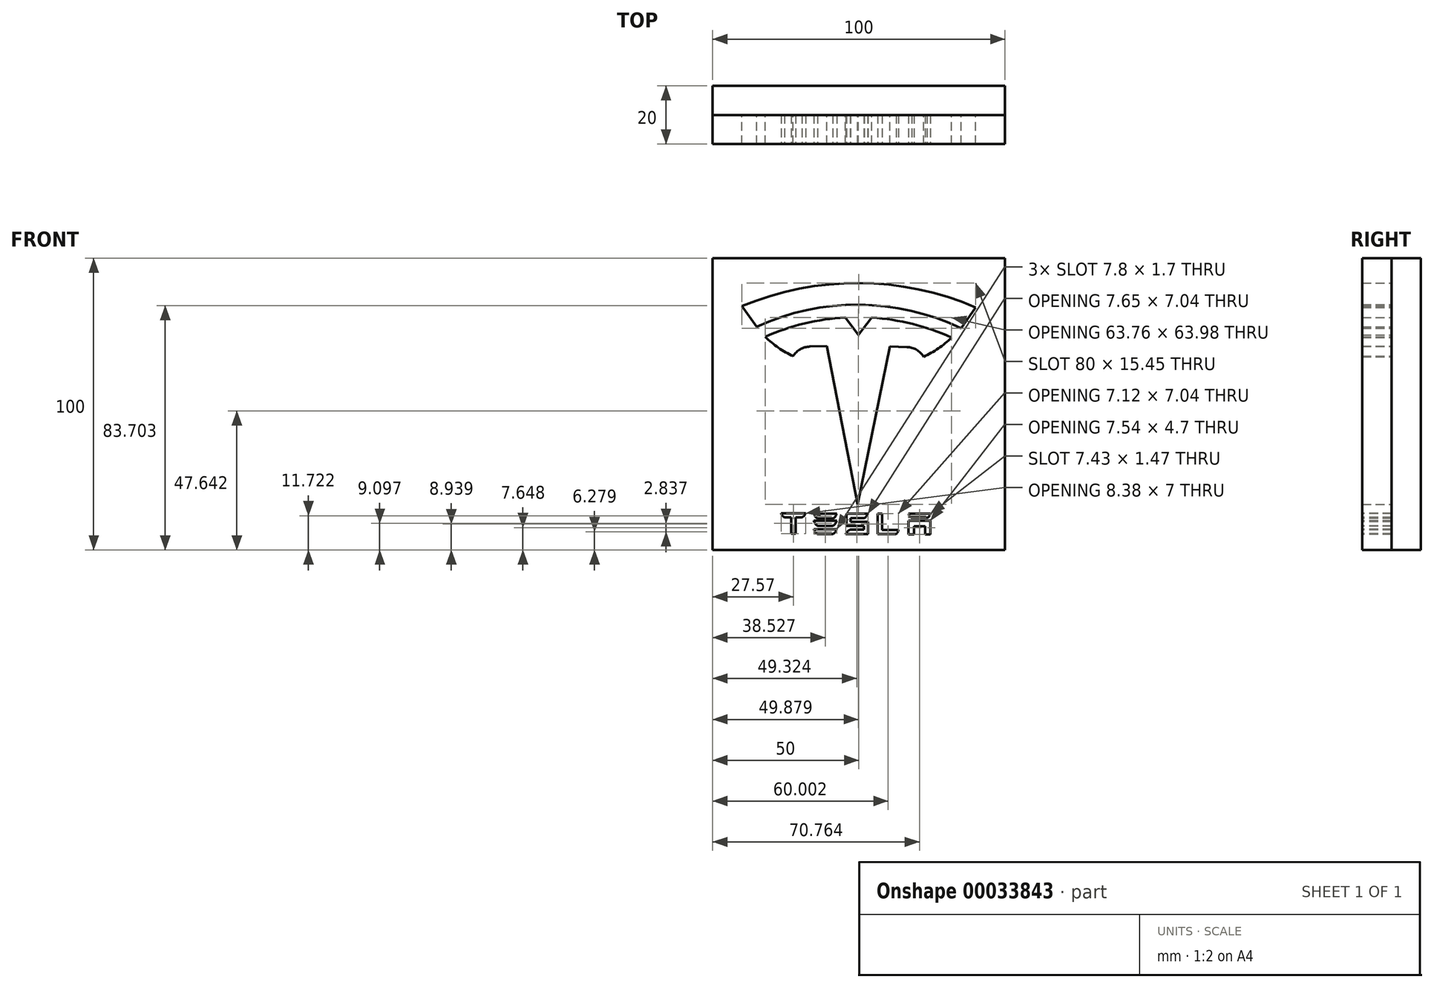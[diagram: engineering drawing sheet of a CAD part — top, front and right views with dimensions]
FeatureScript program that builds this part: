
annotation { "Feature Type Name" : "Feature", "Feature Type Description" : "" }
export const myFeature = defineFeature(function(context is Context, id is Id, definition is map)
    precondition{}
    {
        {
            var Q0;
            Q0=qCreatedBy(makeId("Front.planeOp"),FACE);
            var sketch = newSketch(context, id + "F0", { "sketchPlane" : qUnion([Q0])});
            skLineSegment(sketch, "E0.rect.bottom", {"start": v(50, 50) * mm, "end": v(-50, 50) * mm});
            skLineSegment(sketch, "E0.rect.top", {"start": v(50, -50) * mm, "end": v(-50, -50) * mm});
            skLineSegment(sketch, "E0.rect.left", {"start": v(50, 50) * mm, "end": v(50, -50) * mm});
            skLineSegment(sketch, "E0.rect.right", {"start": v(-50, 50) * mm, "end": v(-50, -50) * mm});
            skPoint(sketch, "E0.rect.middle", {"position": v(0, 0) * mm});
            skSolve(sketch);
        }
        {
            var Q0;
            Q0=makeQuery(id+"F0.imprint","IMPRINT",FACE,{"disambiguationData":[TD([[makeQuery(id+"F0.imprint","IMPRINT",EDGE,{"derivedFrom":sQuery(id+"F0.wireOp",EDGE,"E0.rect.bottom")}),1.0]])]});
            extrude(context, id + "F1", {"entities" : qUnion([Q0]), "depth" : 10 * mm});
        }
        {
            var Q0;
            Q0=makeQuery(id+"F1.opExtrude","CAP_FACE",FACE,{"disambiguationData":[OSD([sQuery(id+"F0.wireOp",EDGE,"E0.rect.bottom"),sQuery(id+"F0.wireOp",EDGE,"E0.rect.top"),sQuery(id+"F0.wireOp",EDGE,"E0.rect.left"),sQuery(id+"F0.wireOp",EDGE,"E0.rect.right")])],"isStart":false});
            var sketch = newSketch(context, id + "F2", { "sketchPlane" : qUnion([Q0])});
            skArc(sketch, "E1", {"start": v(40, 33.1) * mm, "mid": v(0.04, 41.43) * mm, "end": v(-40, 33.52) * mm});
            skArc(sketch, "E2", {"start": v(35, 25.98) * mm, "mid": v(0.05, 34.02) * mm, "end": v(-35, 26.39) * mm});
            skLineSegment(sketch, "E3", {"start": v(0, 50) * mm, "end": v(-0.44, -48.04) * mm, "construction": true});
            skLineSegment(sketch, "E4", {"start": v(35, 25.98) * mm, "end": v(40, 33.1) * mm});
            skLineSegment(sketch, "E5", {"start": v(-35, 26.39) * mm, "end": v(-40, 33.52) * mm});
            skArc(sketch, "E6", {"start": v(32, 22.62) * mm, "mid": v(31.87, 22.68) * mm, "end": v(31.75, 22.74) * mm});
            skArc(sketch, "E7", {"start": v(-32, 23.03) * mm, "mid": v(-27.53, 19.3) * mm, "end": v(-22.5, 16.38) * mm});
            skArc(sketch, "E8.MirrorCS", {"start": v(31.76, 22.75) * mm, "mid": v(27.26, 19.05) * mm, "end": v(22.2, 16.18) * mm});
            skArc(sketch, "E9.trimOffspring", {"start": v(-4.58, 29.63) * mm, "mid": v(-18.6, 27.59) * mm, "end": v(-32, 23.03) * mm});
            skArc(sketch, "E10.MirrorCS", {"start": v(4.4, 29.6) * mm, "mid": v(18.4, 27.42) * mm, "end": v(31.76, 22.75) * mm});
            skArc(sketch, "E11", {"start": v(-16.74, 19.67) * mm, "mid": v(-20.03, 18.75) * mm, "end": v(-22.5, 16.38) * mm});
            skLineSegment(sketch, "E12", {"start": v(-16.74, 19.67) * mm, "end": v(-10.89, 19.82) * mm});
            skLineSegment(sketch, "E13", {"start": v(-10.89, 19.82) * mm, "end": v(-0.38, -34.35) * mm});
            skArc(sketch, "E14.MirrorCS", {"start": v(16.47, 19.52) * mm, "mid": v(19.75, 18.57) * mm, "end": v(22.2, 16.18) * mm});
            skLineSegment(sketch, "E15.MirrorCS", {"start": v(16.47, 19.52) * mm, "end": v(10.62, 19.72) * mm});
            skLineSegment(sketch, "E16.MirrorCS", {"start": v(10.62, 19.72) * mm, "end": v(-0.38, -34.35) * mm});
            skLineSegment(sketch, "E17", {"start": v(-4.58, 29.63) * mm, "end": v(-0.12, 23.62) * mm});
            skLineSegment(sketch, "E18.MirrorCS", {"start": v(4.4, 29.6) * mm, "end": v(-0.12, 23.62) * mm});
            skPoint(sketch, "E19.orphan", {"position": v(-0.1, 29.74) * mm});
            skSolve(sketch);
        }
        {
            var Q0;
            Q0=makeQuery(id+"F2.imprint","IMPRINT",FACE,{"disambiguationData":[TD([[makeQuery(id+"F2.imprint","IMPRINT",EDGE,{"derivedFrom":sQuery(id+"F2.wireOp",EDGE,"E1")}),-1.0]])]});
            extrude(context, id + "F3", {"entities" : qUnion([Q0]), "depth" : 10 * mm});
        }
        {
            var Q0;
            Q0=makeQuery(id+"F3.opExtrude","CAP_FACE",FACE,{"disambiguationData":[OSD([sQuery(id+"F0.wireOp",EDGE,"E0.rect.bottom"),sQuery(id+"F0.wireOp",EDGE,"E0.rect.top"),sQuery(id+"F0.wireOp",EDGE,"E0.rect.left"),sQuery(id+"F0.wireOp",EDGE,"E0.rect.right"),sQuery(id+"F2.wireOp",EDGE,"E1"),sQuery(id+"F2.wireOp",EDGE,"E2"),sQuery(id+"F2.wireOp",EDGE,"E4"),sQuery(id+"F2.wireOp",EDGE,"E5"),sQuery(id+"F2.wireOp",EDGE,"E7"),sQuery(id+"F2.wireOp",EDGE,"E8.MirrorCS"),sQuery(id+"F2.wireOp",EDGE,"E9.trimOffspring"),sQuery(id+"F2.wireOp",EDGE,"E10.MirrorCS"),sQuery(id+"F2.wireOp",EDGE,"E11"),sQuery(id+"F2.wireOp",EDGE,"E12"),sQuery(id+"F2.wireOp",EDGE,"E13"),sQuery(id+"F2.wireOp",EDGE,"E14.MirrorCS"),sQuery(id+"F2.wireOp",EDGE,"E15.MirrorCS"),sQuery(id+"F2.wireOp",EDGE,"E16.MirrorCS"),sQuery(id+"F2.wireOp",EDGE,"E17"),sQuery(id+"F2.wireOp",EDGE,"E18.MirrorCS")])],"isStart":false});
            var sketch = newSketch(context, id + "F4", { "sketchPlane" : qUnion([Q0])});
            skLineSegment(sketch, "E20", {"start": v(-26.62, -37.4) * mm, "end": v(-18.24, -37.4) * mm});
            skArc(sketch, "E21", {"start": v(-26.62, -37.4) * mm, "mid": v(-26.2, -38.25) * mm, "end": v(-25.42, -38.82) * mm});
            skLineSegment(sketch, "E22", {"start": v(-22.43, -37.4) * mm, "end": v(-22.43, -44.4) * mm, "construction": true});
            skArc(sketch, "E23.MirrorCS", {"start": v(-18.24, -37.4) * mm, "mid": v(-18.67, -38.25) * mm, "end": v(-19.44, -38.82) * mm});
            skLineSegment(sketch, "E24", {"start": v(-25.42, -38.82) * mm, "end": v(-23.2, -38.82) * mm});
            skLineSegment(sketch, "E25", {"start": v(-23.2, -38.82) * mm, "end": v(-23.2, -44.4) * mm});
            skLineSegment(sketch, "E26", {"start": v(-23.2, -44.4) * mm, "end": v(-22.43, -44.4) * mm});
            skLineSegment(sketch, "E27.MirrorCS", {"start": v(-19.44, -38.82) * mm, "end": v(-21.67, -38.82) * mm});
            skLineSegment(sketch, "E28.MirrorCS", {"start": v(-21.67, -38.82) * mm, "end": v(-21.67, -44.4) * mm});
            skLineSegment(sketch, "E29.MirrorCS", {"start": v(-21.67, -44.4) * mm, "end": v(-22.43, -44.4) * mm});
            skLineSegment(sketch, "E30", {"start": v(-15.37, -37.56) * mm, "end": v(-11.47, -37.56) * mm});
            skArc(sketch, "E31", {"start": v(-15.37, -37.56) * mm, "mid": v(-14.9, -38.54) * mm, "end": v(-14.09, -39.26) * mm});
            skLineSegment(sketch, "E32", {"start": v(-11.47, -37.56) * mm, "end": v(-11.47, -45.21) * mm, "construction": true});
            skLineSegment(sketch, "E33", {"start": v(-14.09, -39.26) * mm, "end": v(-11.47, -39.26) * mm});
            skLineSegment(sketch, "E34", {"start": v(-15.37, -40.03) * mm, "end": v(-11.47, -40.03) * mm});
            skArc(sketch, "E35", {"start": v(-15.37, -40.03) * mm, "mid": v(-14.9, -41.01) * mm, "end": v(-14.09, -41.73) * mm});
            skLineSegment(sketch, "E36", {"start": v(-14.09, -41.73) * mm, "end": v(-11.47, -41.73) * mm});
            skLineSegment(sketch, "E37", {"start": v(-15.37, -42.87) * mm, "end": v(-11.47, -42.87) * mm});
            skArc(sketch, "E38", {"start": v(-15.37, -42.87) * mm, "mid": v(-14.9, -43.85) * mm, "end": v(-14.09, -44.57) * mm});
            skLineSegment(sketch, "E39", {"start": v(-14.09, -44.57) * mm, "end": v(-11.47, -44.57) * mm});
            skArc(sketch, "E40.MirrorCS", {"start": v(-7.57, -37.56) * mm, "mid": v(-8.05, -38.54) * mm, "end": v(-8.86, -39.26) * mm});
            skLineSegment(sketch, "E41.MirrorCS", {"start": v(-8.86, -39.26) * mm, "end": v(-11.47, -39.26) * mm});
            skLineSegment(sketch, "E42.MirrorCS", {"start": v(-7.57, -40.03) * mm, "end": v(-11.47, -40.03) * mm});
            skArc(sketch, "E43.MirrorCS", {"start": v(-7.57, -40.03) * mm, "mid": v(-8.05, -41.01) * mm, "end": v(-8.86, -41.73) * mm});
            skLineSegment(sketch, "E44.MirrorCS", {"start": v(-8.86, -41.73) * mm, "end": v(-11.47, -41.73) * mm});
            skLineSegment(sketch, "E45.MirrorCS", {"start": v(-7.57, -42.87) * mm, "end": v(-11.47, -42.87) * mm});
            skArc(sketch, "E46.MirrorCS", {"start": v(-7.57, -42.87) * mm, "mid": v(-8.05, -43.85) * mm, "end": v(-8.86, -44.57) * mm});
            skLineSegment(sketch, "E47.MirrorCS", {"start": v(-8.86, -44.57) * mm, "end": v(-11.47, -44.57) * mm});
            skLineSegment(sketch, "E48", {"start": v(3.06, -37.54) * mm, "end": v(-4.19, -37.54) * mm});
            skLineSegment(sketch, "E49", {"start": v(-4.19, -37.54) * mm, "end": v(-4.19, -41.7) * mm});
            skLineSegment(sketch, "E50", {"start": v(-4.19, -41.7) * mm, "end": v(1.75, -41.7) * mm});
            skLineSegment(sketch, "E51", {"start": v(1.75, -41.7) * mm, "end": v(1.75, -43.05) * mm});
            skLineSegment(sketch, "E52", {"start": v(1.75, -43.05) * mm, "end": v(-2.97, -43.05) * mm});
            skArc(sketch, "E53", {"start": v(-2.97, -43.05) * mm, "mid": v(-3.89, -43.67) * mm, "end": v(-4.5, -44.58) * mm});
            skLineSegment(sketch, "E54", {"start": v(-4.5, -44.58) * mm, "end": v(3.15, -44.58) * mm});
            skLineSegment(sketch, "E55", {"start": v(3.15, -44.58) * mm, "end": v(3.15, -40.42) * mm});
            skLineSegment(sketch, "E56", {"start": v(3.15, -40.42) * mm, "end": v(-2.79, -40.42) * mm});
            skLineSegment(sketch, "E57", {"start": v(-2.79, -40.42) * mm, "end": v(-2.79, -39.07) * mm});
            skLineSegment(sketch, "E58", {"start": v(-2.79, -39.07) * mm, "end": v(1.93, -39.07) * mm});
            skArc(sketch, "E59", {"start": v(1.93, -39.07) * mm, "mid": v(2.63, -38.4) * mm, "end": v(3.06, -37.54) * mm});
            skPoint(sketch, "E60.orphan", {"position": v(-7.57, -37.56) * mm});
            skLineSegment(sketch, "E61", {"start": v(-11.47, -37.56) * mm, "end": v(-7.57, -37.56) * mm});
            skLineSegment(sketch, "E62", {"start": v(6.44, -37.54) * mm, "end": v(6.44, -44.58) * mm});
            skLineSegment(sketch, "E63", {"start": v(6.44, -44.58) * mm, "end": v(12.74, -44.58) * mm});
            skLineSegment(sketch, "E64", {"start": v(6.44, -37.54) * mm, "end": v(7.93, -37.54) * mm});
            skLineSegment(sketch, "E65", {"start": v(7.93, -37.54) * mm, "end": v(7.93, -43.2) * mm});
            skLineSegment(sketch, "E66", {"start": v(7.93, -43.2) * mm, "end": v(13.56, -43.2) * mm});
            skArc(sketch, "E67", {"start": v(12.74, -44.58) * mm, "mid": v(13.28, -43.97) * mm, "end": v(13.56, -43.2) * mm});
            skLineSegment(sketch, "E68", {"start": v(20.76, -37.5) * mm, "end": v(20.76, -45.16) * mm, "construction": true});
            skLineSegment(sketch, "E69", {"start": v(17.05, -37.54) * mm, "end": v(20.76, -37.54) * mm});
            skArc(sketch, "E70", {"start": v(17.05, -37.54) * mm, "mid": v(17.4, -38.43) * mm, "end": v(18.15, -39.01) * mm});
            skLineSegment(sketch, "E71", {"start": v(18.15, -39.01) * mm, "end": v(20.76, -39.01) * mm});
            skLineSegment(sketch, "E72", {"start": v(20.76, -40) * mm, "end": v(17, -40) * mm});
            skLineSegment(sketch, "E73", {"start": v(17, -40) * mm, "end": v(17, -44.7) * mm});
            skLineSegment(sketch, "E74", {"start": v(17, -44.7) * mm, "end": v(18.86, -44.7) * mm});
            skLineSegment(sketch, "E75", {"start": v(18.86, -44.7) * mm, "end": v(18.86, -41.85) * mm});
            skLineSegment(sketch, "E76", {"start": v(18.86, -41.85) * mm, "end": v(20.76, -41.85) * mm});
            skLineSegment(sketch, "E77.MirrorCS", {"start": v(24.48, -37.54) * mm, "end": v(20.76, -37.54) * mm});
            skArc(sketch, "E78.MirrorCS", {"start": v(24.48, -37.54) * mm, "mid": v(24.13, -38.43) * mm, "end": v(23.38, -39.01) * mm});
            skLineSegment(sketch, "E79.MirrorCS", {"start": v(23.38, -39.01) * mm, "end": v(20.76, -39.01) * mm});
            skLineSegment(sketch, "E80.MirrorCS", {"start": v(20.76, -40) * mm, "end": v(24.53, -40) * mm});
            skLineSegment(sketch, "E81.MirrorCS", {"start": v(24.53, -40) * mm, "end": v(24.53, -44.7) * mm});
            skLineSegment(sketch, "E82.MirrorCS", {"start": v(24.53, -44.7) * mm, "end": v(22.67, -44.7) * mm});
            skLineSegment(sketch, "E83.MirrorCS", {"start": v(22.67, -44.7) * mm, "end": v(22.67, -41.85) * mm});
            skLineSegment(sketch, "E84.MirrorCS", {"start": v(22.67, -41.85) * mm, "end": v(20.76, -41.85) * mm});
            skSolve(sketch);
        }
        {
            var Q0;
            Q0=makeQuery(id+"F4.imprint","IMPRINT",FACE,{"disambiguationData":[TD([[makeQuery(id+"F4.imprint","IMPRINT",EDGE,{"derivedFrom":sQuery(id+"F4.wireOp",EDGE,"E20")}),-1.0]])]});
            var Q1;
            Q1=makeQuery(id+"F4.imprint","IMPRINT",FACE,{"disambiguationData":[TD([[makeQuery(id+"F4.imprint","IMPRINT",EDGE,{"derivedFrom":sQuery(id+"F4.wireOp",EDGE,"E30")}),-1.0]])]});
            var Q2;
            Q2=makeQuery(id+"F4.imprint","IMPRINT",FACE,{"disambiguationData":[TD([[makeQuery(id+"F4.imprint","IMPRINT",EDGE,{"derivedFrom":sQuery(id+"F4.wireOp",EDGE,"E34")}),-1.0]])]});
            var Q3;
            Q3=makeQuery(id+"F4.imprint","IMPRINT",FACE,{"disambiguationData":[TD([[makeQuery(id+"F4.imprint","IMPRINT",EDGE,{"derivedFrom":sQuery(id+"F4.wireOp",EDGE,"E37")}),-1.0]])]});
            var Q4;
            Q4=makeQuery(id+"F4.imprint","IMPRINT",FACE,{"disambiguationData":[TD([[makeQuery(id+"F4.imprint","IMPRINT",EDGE,{"derivedFrom":sQuery(id+"F4.wireOp",EDGE,"E48")}),1.0]])]});
            var Q5;
            Q5=makeQuery(id+"F4.imprint","IMPRINT",FACE,{"disambiguationData":[TD([[makeQuery(id+"F4.imprint","IMPRINT",EDGE,{"derivedFrom":sQuery(id+"F4.wireOp",EDGE,"E62")}),1.0]])]});
            var Q6;
            Q6=makeQuery(id+"F4.imprint","IMPRINT",FACE,{"disambiguationData":[TD([[makeQuery(id+"F4.imprint","IMPRINT",EDGE,{"derivedFrom":sQuery(id+"F4.wireOp",EDGE,"E72")}),1.0]])]});
            var Q7;
            Q7=makeQuery(id+"F4.imprint","IMPRINT",FACE,{"disambiguationData":[TD([[makeQuery(id+"F4.imprint","IMPRINT",EDGE,{"derivedFrom":sQuery(id+"F4.wireOp",EDGE,"E69")}),-1.0]])]});
            extrude(context, id + "F5", {"entities" : qUnion([Q0, Q1, Q2, Q3, Q4, Q5, Q6, Q7]), "operationType" : NewBodyOperationType.REMOVE, "oppositeDirection" : true, "depth" : 10 * mm});
        }
    });
